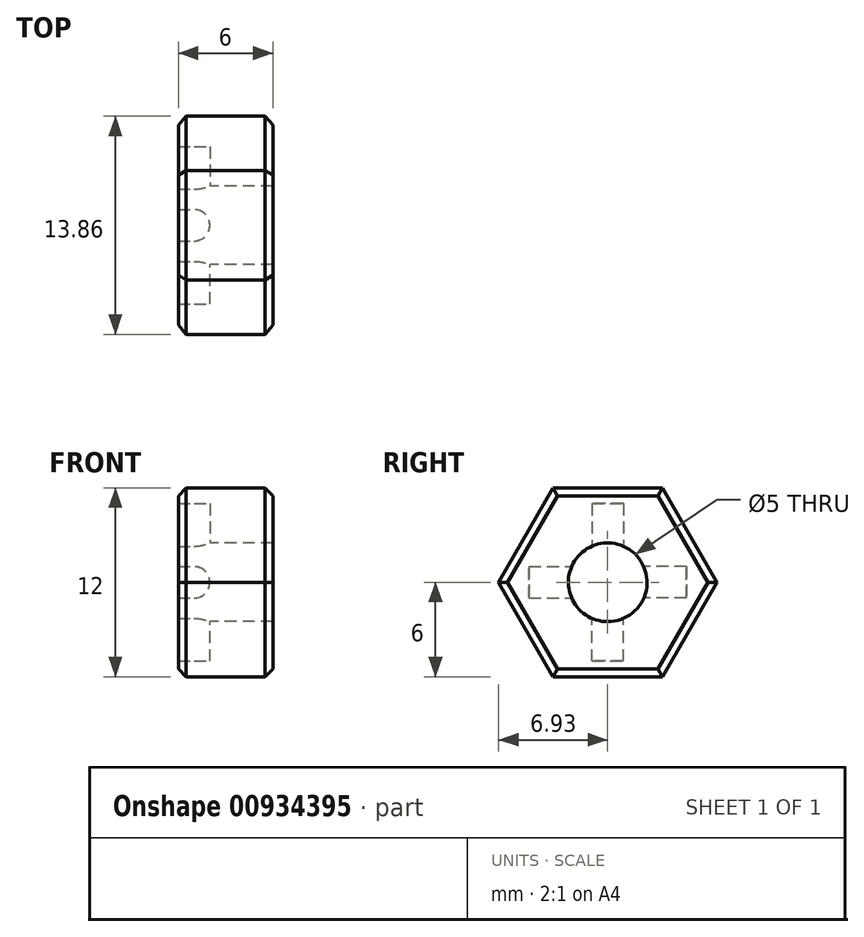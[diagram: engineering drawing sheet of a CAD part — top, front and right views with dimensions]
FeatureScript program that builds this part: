
annotation { "Feature Type Name" : "Feature", "Feature Type Description" : "" }
export const myFeature = defineFeature(function(context is Context, id is Id, definition is map)
    precondition{}
    {
        {
            var Q0;
            Q0=qCreatedBy(makeId("Right.planeOp"),FACE);
            var sketch = newSketch(context, id + "F0", { "sketchPlane" : qUnion([Q0])});
            skCircle(sketch, "E0.cCircle", {"center": v(0, 0) * mm, "radius": 6 * mm, "construction": true});
            skLineSegment(sketch, "E0.0", {"start": v(-3.46, 6) * mm, "end": v(3.46, 6) * mm});
            skLineSegment(sketch, "E0.1", {"start": v(3.46, 6) * mm, "end": v(6.93, 0) * mm});
            skLineSegment(sketch, "E0.2", {"start": v(6.93, 0) * mm, "end": v(3.46, -6) * mm});
            skLineSegment(sketch, "E0.3", {"start": v(3.46, -6) * mm, "end": v(-3.46, -6) * mm});
            skLineSegment(sketch, "E0.4", {"start": v(-3.46, -6) * mm, "end": v(-6.93, 0) * mm});
            skLineSegment(sketch, "E0.5", {"start": v(-6.93, 0) * mm, "end": v(-3.46, 6) * mm});
            skPoint(sketch, "E0.0.midPoint", {"position": v(0, 6) * mm});
            skCircle(sketch, "E1", {"center": v(0, 0) * mm, "radius": 2.5 * mm});
            skSolve(sketch);
        }
        {
            var Q0;
            Q0=qCreatedBy(makeId("Front.planeOp"),FACE);
            var sketch = newSketch(context, id + "F1", { "sketchPlane" : qUnion([Q0])});
            skCircle(sketch, "E2", {"center": v(0, 0) * mm, "radius": 1 * mm});
            skSolve(sketch);
        }
        {
            var Q0;
            Q0=qCreatedBy(makeId("Top.planeOp"),FACE);
            var sketch = newSketch(context, id + "F2", { "sketchPlane" : qUnion([Q0])});
            skCircle(sketch, "E3", {"center": v(0, 0) * mm, "radius": 1 * mm});
            skSolve(sketch);
        }
        {
            var Q0;
            Q0=makeQuery(id+"F0.imprint","IMPRINT",FACE,{"disambiguationData":[TD([[makeQuery(id+"F0.imprint","IMPRINT",EDGE,{"derivedFrom":sQuery(id+"F0.wireOp",EDGE,"E0.0")}),-1.0]])]});
            extrude(context, id + "F3", {"entities" : qUnion([Q0]), "depth" : 5 * mm, "offsetDistance" : 25 * mm});
        }
        {
            var Q0;
            Q0=makeQuery(id+"F1.imprint","IMPRINT",FACE,{"disambiguationData":[TD([[makeQuery(id+"F1.imprint","IMPRINT",EDGE,{"derivedFrom":sQuery(id+"F1.wireOp",EDGE,"E2")}),1.0]])]});
            extrude(context, id + "F4", {"entities" : qUnion([Q0]), "operationType" : NewBodyOperationType.REMOVE, "oppositeDirection" : true, "depth" : 5 * mm, "offsetDistance" : 25 * mm});
        }
        {
            var Q0;
            Q0 = qSketchRegion(id + "F1", true);
            extrude(context, id + "F5", {"entities" : qUnion([Q0]), "operationType" : NewBodyOperationType.REMOVE, "depth" : 5 * mm, "offsetDistance" : 25 * mm});
        }
        {
            var Q0;
            Q0 = qSketchRegion(id + "F2", true);
            extrude(context, id + "F6", {"entities" : qUnion([Q0]), "operationType" : NewBodyOperationType.REMOVE, "oppositeDirection" : true, "depth" : 5 * mm, "offsetDistance" : 25 * mm});
        }
        {
            var Q0;
            Q0 = qSketchRegion(id + "F2", true);
            extrude(context, id + "F7", {"entities" : qUnion([Q0]), "operationType" : NewBodyOperationType.REMOVE, "depth" : 5 * mm, "offsetDistance" : 25 * mm});
        }
        {
            var Q0;
            Q0=makeQuery(id+"F3.opExtrude","CAP_EDGE",EDGE,{"disambiguationData":[OSD([sQuery(id+"F0.wireOp",EDGE,"E0.3")])],"isStart":false});
            var Q1;
            Q1=makeQuery(id+"F3.opExtrude","CAP_EDGE",EDGE,{"disambiguationData":[OSD([sQuery(id+"F0.wireOp",EDGE,"E0.2")])],"isStart":false});
            var Q2;
            Q2=makeQuery(id+"F3.opExtrude","CAP_EDGE",EDGE,{"disambiguationData":[OSD([sQuery(id+"F0.wireOp",EDGE,"E0.1")])],"isStart":false});
            var Q3;
            Q3=makeQuery(id+"F3.opExtrude","CAP_EDGE",EDGE,{"disambiguationData":[OSD([sQuery(id+"F0.wireOp",EDGE,"E0.0")])],"isStart":false});
            var Q4;
            Q4=makeQuery(id+"F3.opExtrude","CAP_EDGE",EDGE,{"disambiguationData":[OSD([sQuery(id+"F0.wireOp",EDGE,"E0.5")])],"isStart":false});
            var Q5;
            Q5=makeQuery(id+"F3.opExtrude","CAP_EDGE",EDGE,{"disambiguationData":[OSD([sQuery(id+"F0.wireOp",EDGE,"E0.4")])],"isStart":false});
            chamfer(context, id + "F8", {"entities" : qUnion([Q0, Q1, Q2, Q3, Q4, Q5]), "width" : 0.5 * mm, "tangentPropagation" : true});
        }
        {
            var Q0;
            Q0=makeQuery(id+"F3.opExtrude","CAP_FACE",FACE,{"disambiguationData":[OSD([sQuery(id+"F0.wireOp",EDGE,"E0.0"),sQuery(id+"F0.wireOp",EDGE,"E0.1"),sQuery(id+"F0.wireOp",EDGE,"E0.2"),sQuery(id+"F0.wireOp",EDGE,"E0.3"),sQuery(id+"F0.wireOp",EDGE,"E0.4"),sQuery(id+"F0.wireOp",EDGE,"E0.5"),sQuery(id+"F0.wireOp",EDGE,"E1")])],"isStart":true});
            extrude(context, id + "F9", {"entities" : qUnion([Q0]), "operationType" : NewBodyOperationType.ADD, "depth" : 1 * mm, "offsetDistance" : 25 * mm});
        }
        {
            var Q0;
            Q0=makeQuery(id+"F9.opExtrude","CAP_EDGE",EDGE,{"disambiguationData":[OSD([sQuery(id+"F0.wireOp",EDGE,"E0.4")])],"isStart":false});
            var Q1;
            Q1=makeQuery(id+"F9.opExtrude","CAP_EDGE",EDGE,{"disambiguationData":[OSD([sQuery(id+"F0.wireOp",EDGE,"E0.2")])],"isStart":false});
            var Q2;
            Q2=makeQuery(id+"F9.opExtrude","CAP_EDGE",EDGE,{"disambiguationData":[OSD([sQuery(id+"F0.wireOp",EDGE,"E0.3")])],"isStart":false});
            var Q3;
            Q3=makeQuery(id+"F9.opExtrude","CAP_EDGE",EDGE,{"disambiguationData":[OSD([sQuery(id+"F0.wireOp",EDGE,"E0.0")])],"isStart":false});
            var Q4;
            Q4=makeQuery(id+"F9.opExtrude","CAP_EDGE",EDGE,{"disambiguationData":[OSD([sQuery(id+"F0.wireOp",EDGE,"E0.1")])],"isStart":false});
            var Q5;
            Q5=makeQuery(id+"F9.opExtrude","CAP_EDGE",EDGE,{"disambiguationData":[OSD([sQuery(id+"F0.wireOp",EDGE,"E0.5")])],"isStart":false});
            chamfer(context, id + "F10", {"entities" : qUnion([Q0, Q1, Q2, Q3, Q4, Q5]), "width" : 0.5 * mm, "tangentPropagation" : true});
        }
    });
